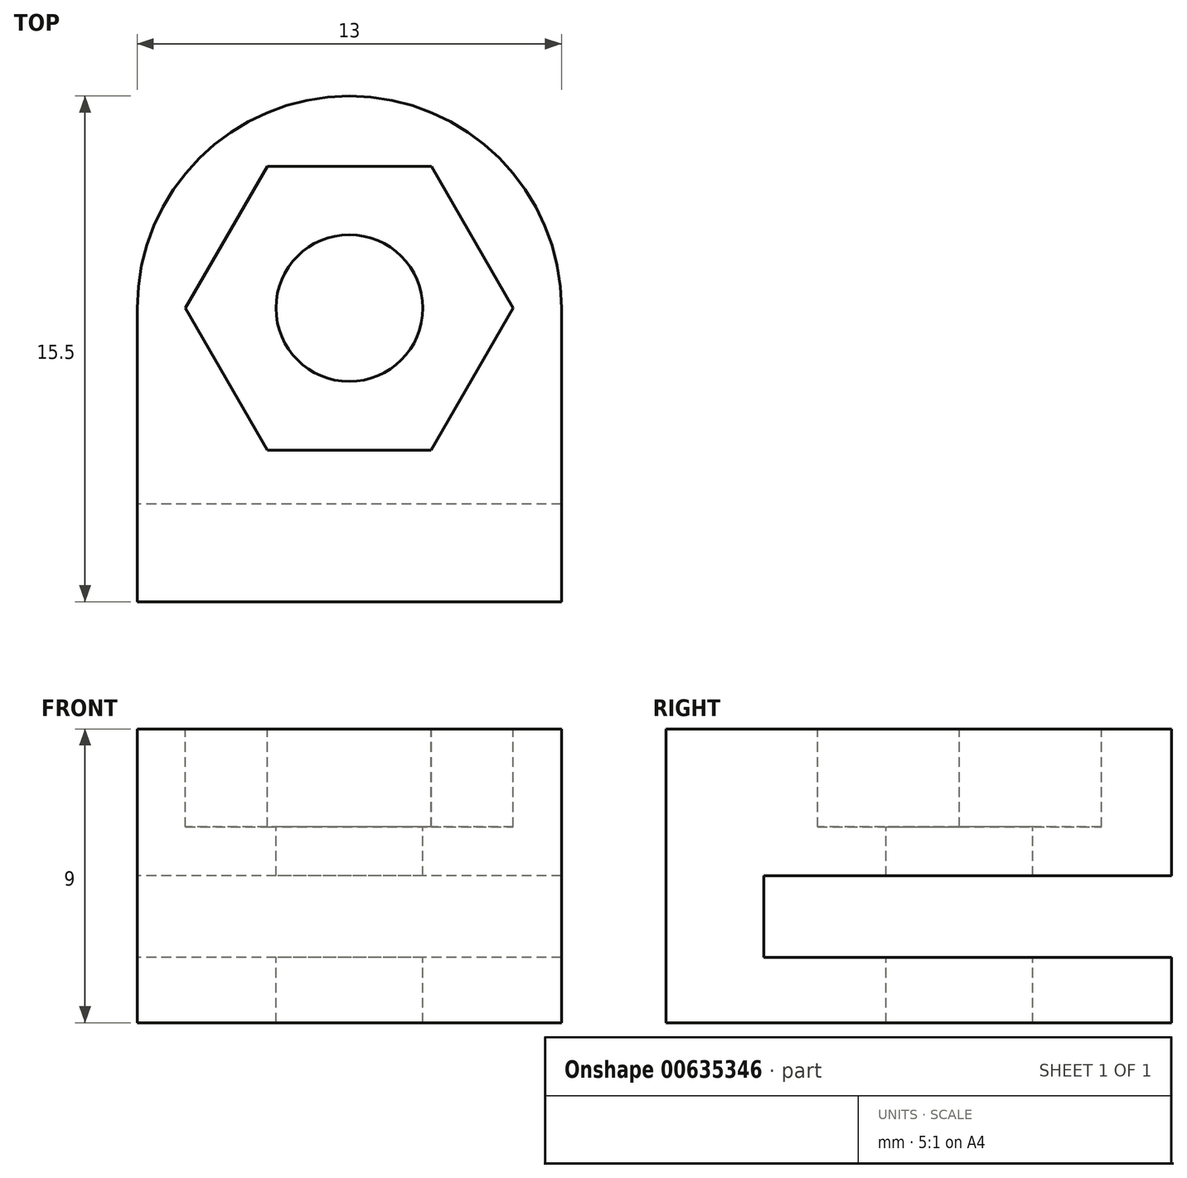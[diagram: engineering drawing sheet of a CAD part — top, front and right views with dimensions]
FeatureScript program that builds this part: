
annotation { "Feature Type Name" : "Feature", "Feature Type Description" : "" }
export const myFeature = defineFeature(function(context is Context, id is Id, definition is map)
    precondition{}
    {
        {
            var Q0;
            Q0=qCreatedBy(makeId("Top.planeOp"),FACE);
            var sketch = newSketch(context, id + "F0", { "sketchPlane" : qUnion([Q0])});
            skLineSegment(sketch, "E0", {"start": v(0, 0) * mm, "end": v(0, -9) * mm});
            skLineSegment(sketch, "E1", {"start": v(0, -9) * mm, "end": v(13, -9) * mm});
            skLineSegment(sketch, "E2", {"start": v(13, -9) * mm, "end": v(13, 0) * mm});
            skArc(sketch, "E3", {"start": v(0, 0) * mm, "mid": v(6.5, 6.5) * mm, "end": v(13, 0) * mm});
            skSolve(sketch);
        }
        {
            var Q0;
            Q0=makeQuery(id+"F0.imprint","IMPRINT",FACE,{"disambiguationData":[TD([[makeQuery(id+"F0.imprint","IMPRINT",EDGE,{"derivedFrom":sQuery(id+"F0.wireOp",EDGE,"E0")}),1.0]])]});
            extrude(context, id + "F1", {"entities" : qUnion([Q0]), "depth" : 9 * mm, "offsetDistance" : 25.4 * mm});
        }
        {
            var Q0;
            Q0=makeQuery(id+"F1.opExtrude","CAP_FACE",FACE,{"disambiguationData":[OSD([sQuery(id+"F0.wireOp",EDGE,"E0"),sQuery(id+"F0.wireOp",EDGE,"E1"),sQuery(id+"F0.wireOp",EDGE,"E2"),sQuery(id+"F0.wireOp",EDGE,"E3")])],"isStart":false});
            var sketch = newSketch(context, id + "F2", { "sketchPlane" : qUnion([Q0])});
            skCircle(sketch, "E4.cCircle", {"center": v(6.5, 0) * mm, "radius": 4.35 * mm, "construction": true});
            skLineSegment(sketch, "E4.0", {"start": v(9.01, 4.35) * mm, "end": v(11.52, 0) * mm});
            skLineSegment(sketch, "E4.1", {"start": v(11.52, 0) * mm, "end": v(9.01, -4.35) * mm});
            skLineSegment(sketch, "E4.2", {"start": v(9.01, -4.35) * mm, "end": v(3.99, -4.35) * mm});
            skLineSegment(sketch, "E4.3", {"start": v(3.99, -4.35) * mm, "end": v(1.48, 0) * mm});
            skLineSegment(sketch, "E4.4", {"start": v(1.48, 0) * mm, "end": v(3.99, 4.35) * mm});
            skLineSegment(sketch, "E4.5", {"start": v(3.99, 4.35) * mm, "end": v(9.01, 4.35) * mm});
            skPoint(sketch, "E4.0.midPoint", {"position": v(10.27, 2.17) * mm});
            skSolve(sketch);
        }
        {
            var Q0;
            Q0=makeQuery(id+"F2.imprint","IMPRINT",FACE,{"disambiguationData":[TD([[makeQuery(id+"F2.imprint","IMPRINT",EDGE,{"derivedFrom":sQuery(id+"F2.wireOp",EDGE,"E4.0")}),-1.0]])]});
            extrude(context, id + "F3", {"entities" : qUnion([Q0]), "operationType" : NewBodyOperationType.REMOVE, "oppositeDirection" : true, "depth" : 3 * mm, "offsetDistance" : 25.4 * mm});
        }
        {
            var Q0;
            Q0=makeQuery(id+"F1.opExtrude","CAP_FACE",FACE,{"disambiguationData":[OSD([sQuery(id+"F0.wireOp",EDGE,"E0"),sQuery(id+"F0.wireOp",EDGE,"E1"),sQuery(id+"F0.wireOp",EDGE,"E2"),sQuery(id+"F0.wireOp",EDGE,"E3")])],"isStart":false});
            var sketch = newSketch(context, id + "F4", { "sketchPlane" : qUnion([Q0])});
            skCircle(sketch, "E5", {"center": v(6.5, 0) * mm, "radius": 2.25 * mm});
            skSolve(sketch);
        }
        {
            var Q0;
            Q0=makeQuery(id+"F4.imprint","IMPRINT",FACE,{"disambiguationData":[TD([[makeQuery(id+"F4.imprint","IMPRINT",EDGE,{"derivedFrom":sQuery(id+"F4.wireOp",EDGE,"E5")}),1.0]])]});
            extrude(context, id + "F5", {"entities" : qUnion([Q0]), "operationType" : NewBodyOperationType.REMOVE, "oppositeDirection" : true, "depth" : 25.4 * mm, "offsetDistance" : 25.4 * mm});
        }
        {
            var Q0;
            Q0=makeQuery(id+"F1.opExtrude","SWEPT_FACE",FACE,{"disambiguationData":[OSD([sQuery(id+"F0.wireOp",EDGE,"E0")])]});
            var sketch = newSketch(context, id + "F6", { "sketchPlane" : qUnion([Q0])});
            skLineSegment(sketch, "E6.bottom", {"start": v(6, 4.5) * mm, "end": v(-16.77, 4.5) * mm});
            skLineSegment(sketch, "E6.top", {"start": v(6, 2) * mm, "end": v(-16.77, 2) * mm});
            skLineSegment(sketch, "E6.left", {"start": v(6, 4.5) * mm, "end": v(6, 2) * mm});
            skLineSegment(sketch, "E6.right", {"start": v(-16.77, 4.5) * mm, "end": v(-16.77, 2) * mm});
            skSolve(sketch);
        }
        {
            var Q0;
            {var subQ0=sQuery(id+"F6.wireOp",EDGE,"E6.right");Q0=makeQuery(id+"F6.imprint","IMPRINT",FACE,{"disambiguationData":[TD([[makeQuery(id+"F6.imprint","IMPRINT",EDGE,{"derivedFrom":subQ0}),1.0]])]});}
            var Q1;
            {var subQ0=sQuery(id+"F6.wireOp",EDGE,"E6.left");Q1=makeQuery(id+"F6.imprint","IMPRINT",FACE,{"disambiguationData":[TD([[makeQuery(id+"F6.imprint","IMPRINT",EDGE,{"derivedFrom":subQ0}),-1.0]])]});}
            extrude(context, id + "F7", {"entities" : qUnion([Q0, Q1]), "operationType" : NewBodyOperationType.REMOVE, "oppositeDirection" : true, "depth" : 25 * mm, "offsetDistance" : 25 * mm});
        }
    });
